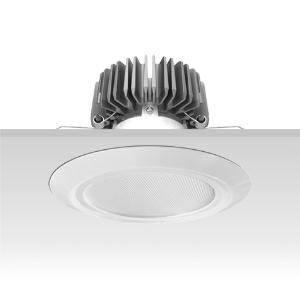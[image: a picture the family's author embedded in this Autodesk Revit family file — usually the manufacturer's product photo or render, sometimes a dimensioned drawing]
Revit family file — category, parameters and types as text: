
# Revit family: 3f_filippi_-_3f_reno_bianco_ampio_3f_filippi_-_30637_a01037_-_3f_reno_200_wh_4000-840_wide___vs_wh_984c
name_source: partatom
category: Lighting Fixtures
units: mm (PartAtom-declared; Revit-internal decimal feet)

## family parameters
Cut with Voids When Loaded = No
Host = Face
Light Source = No
Part Type = Normal
Room Calculation Point = No
Round Connector Dimension = Use Diameter
Shared = No

## types (1)
- 3F Filippi - 3F Reno Bianco Ampio (1 x LED, 3089 lm, 36 W, 4000 K)
    Apparent Load = 36 VA
    Approval mark = CE
    CIE Flux Codes = 75 94 99 100 100
    Color Rendering = 80
    Color Temperature = 4000 K
    Control Gear = Electronic ballast
    Default Elevation = 1800 mm
    Description = ILLUMINOTECHNICAL
Luminous efficiency 100% (DLOR 100%, ULOR 0%).
Initial luminous flux of the luminaire 3089 lm.
Direct symmetric wide distribution.
Installation Interdistance Transv.D = 1.16 x hu - Long.D = 1.14 x hu.
Tabular UGR (CIE 117 - 4H-8H; S=0.25H; 70/50/20): RUG 22.5 - 22.4.
Beam angle: 74° - 74°.
Luminous efficacy 86 lm/W.
Lifetime (L90/B10): 30000 h. (tq+25°C)
Lifetime (L85/B10): 50000 h. (tq+25°C)
Lifetime (L70/B10): 80000 h. (tq+25°C)
Sudden decreased luminous flux after 50000 hours: 0% (C0).
Photobiological safety in compliance with IEC/TR 62778: RG1 low risk, (IEC 62471).
In compliance with IEC/EN 62722-2-1 - IEC/EN 62717 standards.

SOURCE
Compact LED module 4000/840.
Energy efficiency class (UE 2019/2020 - UE 2019/2015): E.
CIE 13.3 Colour rendering index: CRI >80 (R9 <50%).
IES TM-30 Fidelity Index: Rf = 84 Rg = 95.
CCT nominal colour temperature 4000 K.
Colour initial tolerance (MacAdam): SDCM 3.
Zhaga Book 3 compliant.

MECHANICAL
Passive heat dissipator in die-casting aluminium, oversized, for optimum thermal management of the LED module.
Parabolic element with graduated/concentric rings in white polycarbonate.
Transparent external lens with glossy and satin differentiated surfaces, with a cooling and anti-insect system in methacrylate (PMMA).
Fastening spring clips in stainless steel.
Dimensions: diameter 226 mm, height 146 mm. Weight 1.81 kg.
IP44 protection degree for exposed part, IP20 for recessed part.
Mechanical strength to impacts IK06 (1 joule).
Glow-wire test resistance 650°C.

ELECTRICAL
Wiring on a separate unit.
Halogen Free electronic wiring 230V-50/60Hz, power factor 0.95, THD <25%, constant output current, SELV, class II, 1 driver.
Power of the luminaire 36 W.
ENEC - CE.
SAFE FLICKER: PstLM=<1 and SVM=<0.4 (IEC TR 61547-1 and IEC TR 63158), to ensure a more comfortable and safe light.
Luminaire compliant with EN 60598-2-22 for power supply from a centralised emergency system CPSS (Central Power Supply System), not incorporated in the luminaire - high risk areas excluded. The default power and flux are 100% in AC and 100% in DC.
Ambient temperature from 0°C to +25°C.
Temperature class T6 max 85°C.
Relative humidity UR: <85%.

INSTALLATION
Pull-up recessed fitting.
False ceiling carving: 200 mm.
All accessories dedicated to this product are available on the Catalog and on our website www.3F-Filippi.com.

ACCESSORIES
A01037 - Anti-glare microprismatic VS moulded glass, tempered, not flammable, locked and in line with the trim, in white polycarbonate.

APPLICATIONS
Environments: architectural, commercial, exhibition areas, transit areas, corridors, shops, display windows, service areas.
In false ceilings with narrow voids.

WARNING
Luminaire designed for disposal/recycling at end-of-life.
Replaceable (LED only) light source by a professional. Replaceable control gear by a professional.
    Height = 0 mm  [stored 0 ft]
    Lamp = 1 x LED
    Lamp Light Flux = 3089 lm
    Lamp Power = 36 W
    Lamp count = 1
    Length = 226 mm
    Lifetime = 50000 h
    Luminous efficacy = 86 lm/W
    Manufacturer = 3F Filippi
    ModVariant = No
    Model = 3F Filippi - 30637+A01037 - 3F Reno 200 WH 4000-840 WIDE + VS WH
    Mounting Place = Ceiling
    Mounting Type = Recessed
    Number of Poles = 1
    OnlyDefault = Yes
    Power Factor = 1
    Product Name = 3F Filippi - 3F Reno Bianco Ampio
    Product group = recessed luminaire
    ProductGroupID = 4
    Protection Class = Protection class II
    Protection Degree = IP 20
    RLX_Detail_Level = 1
    RLX_Emergency_Light_Flux = 0 lm
    RLX_Emergency_Type = 0
    RLX_Emergency_Type_DB = No
    RlxData = <blob elided: 93717 chars, md5=0cc0722a>
    Socket = socket
    Standby Power = 0 W
    System Light Flux = 3089 lm
    System Power = 36 W
    Type Comments = Product without accessories
    Type Image = 3ffilippi_3f_reno_200_wh_vs_smp.jpg
    URL = http://relux.com
    VarID = ---
    Voltage = 0 V
    Weight = 0.00 kg
    Width = 0 mm  [stored 0 ft]

note: [stored X ft] marks values corroborated as IEEE doubles in the binary element streams (Revit-internal decimal feet)

## geometry (parser evidence)
native form markers: Blend x4, Sweep x11
no freeform markers — native parametric forms only
